# Revit family: QF_ELECTROLUXPROFESSIONAL_1LSNTM_WN6-14_S
name_source: partatom
category: Attrezzature speciali
units: mm (PartAtom-declared; Revit-internal decimal feet)

## family parameters
Basato su piano di lavoro = No
Condiviso = No
Punto di calcolo locali = No
Quota connettore circolare = Usa diametro
Sempre verticale = Sì
Taglio con vuoti quando caricato = No
Tipo di parte = Normale

## types (1)
- 9867730242
    Cycle = 50 Hz
    Depth = 786.6 mm  [stored 2.58071 ft]
    Depth Actual = 790 mm  [stored 2.59186 ft]
    Descrizione = WASHER WN6-14 14KG STEAM 220-240/50/1N COMPASS PRO 6G01 ML 2xWATER POWDER+5xLIQ. EL.VALV.OPEN SST 2.I/O DISCON. STOP
    Gas KW = 0
    Height = 1218.8 mm  [stored 3.99869 ft]
    Height Actual = 1220 mm  [stored 4.00262 ft]
    Item Number = 1L0H9G
    Latent Heat Output = 0.0
    Length Actual = 720 mm  [stored 2.3622 ft]
    Modello = WN6-14
    Phase = 1
    Produttore = Electrolux Professional
    Prospetto di default = 0 mm  [stored 0 ft]
    Sensible Heat Output = 0.0
    Steam Pounds per Hour = 0
    URL = www.electroluxprofessional.com
    Volts = 240 V
    Watts = 800 W
    Weight = 154
    Width = 720 mm  [stored 2.3622 ft]

note: [stored X ft] marks values corroborated as IEEE doubles in the binary element streams (Revit-internal decimal feet)

## geometry (parser evidence)
native form markers: Sweep x4
no freeform markers — native parametric forms only
